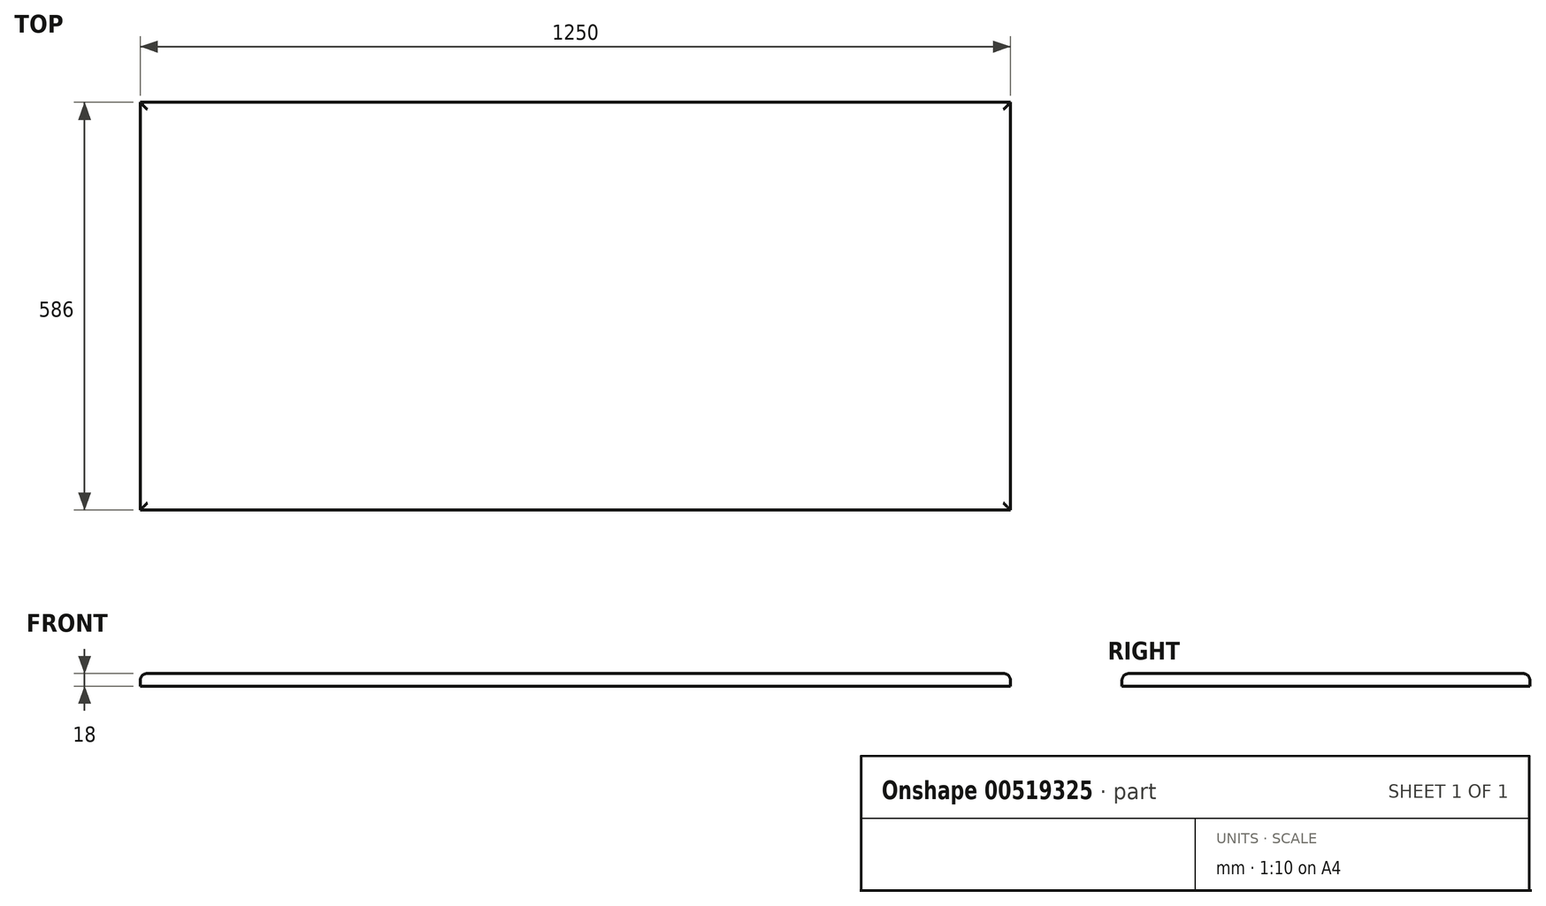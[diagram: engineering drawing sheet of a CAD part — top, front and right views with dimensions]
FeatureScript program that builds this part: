
annotation { "Feature Type Name" : "Feature", "Feature Type Description" : "" }
export const myFeature = defineFeature(function(context is Context, id is Id, definition is map)
    precondition{}
    {
        {
            var Q0;
            Q0=qCreatedBy(makeId("Top.planeOp"),FACE);
            var sketch = newSketch(context, id + "F0", { "sketchPlane" : qUnion([Q0])});
            skLineSegment(sketch, "E0.bottom", {"start": v(625, 293) * mm, "end": v(-625, 293) * mm});
            skLineSegment(sketch, "E0.top", {"start": v(625, -293) * mm, "end": v(-625, -293) * mm});
            skLineSegment(sketch, "E0.left", {"start": v(625, 293) * mm, "end": v(625, -293) * mm});
            skLineSegment(sketch, "E0.right", {"start": v(-625, 293) * mm, "end": v(-625, -293) * mm});
            skPoint(sketch, "E0.middle", {"position": v(0, 0) * mm});
            skSolve(sketch);
        }
        {
            var Q0;
            Q0 = qSketchRegion(id + "F0", true);
            extrude(context, id + "F1", {"entities" : qUnion([Q0]), "depth" : 18 * mm, "offsetDistance" : 25 * mm});
        }
        {
            var Q0;
            Q0=makeQuery(id+"F1.opExtrude","CAP_EDGE",EDGE,{"disambiguationData":[OSD([sQuery(id+"F0.wireOp",EDGE,"E0.top")])],"isStart":false});
            var Q1;
            Q1=makeQuery(id+"F1.opExtrude","CAP_EDGE",EDGE,{"disambiguationData":[OSD([sQuery(id+"F0.wireOp",EDGE,"E0.right")])],"isStart":false});
            var Q2;
            Q2=makeQuery(id+"F1.opExtrude","CAP_EDGE",EDGE,{"disambiguationData":[OSD([sQuery(id+"F0.wireOp",EDGE,"E0.bottom")])],"isStart":false});
            var Q3;
            Q3=makeQuery(id+"F1.opExtrude","CAP_EDGE",EDGE,{"disambiguationData":[OSD([sQuery(id+"F0.wireOp",EDGE,"E0.left")])],"isStart":false});
            fillet(context, id + "F2", {"entities" : qUnion([Q0, Q1, Q2, Q3]), "radius" : 10 * mm, "tangentPropagation" : true, "allowEdgeOverflow" : false});
        }
    });
